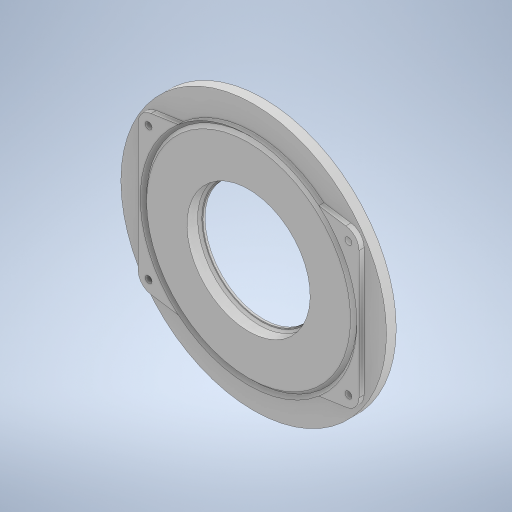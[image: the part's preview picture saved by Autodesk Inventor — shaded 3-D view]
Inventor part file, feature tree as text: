
AUTODESK INVENTOR PART (.ipt)
format: ipt  version: 2023.4 (Build 274418000, 418)  size: 462,336 bytes
history: native  units: mm
features: extrude x14, sketch x8, projected_geometry x3, chamfer x2, mirror x1
ambient origin geometry x8: Origin, YZ Plane, XZ Plane, XY Plane, X Axis, Y Axis, Z Axis, Center Point
bodies: Solid1 (feature_tree)
feature tree (28):
  extrude  "Extrusion1"  Depth=18.0mm TaperAngle=0.0deg
  extrude  "Extrusion5"  Depth=58.0mm
  extrude  "Extrusion8"  Depth=1.5mm
  extrude  "Extrusion9"  Depth=1.0mm TaperAngle=45.0deg
  chamfer  "Chamfer3"  Distance=2.2mm
  extrude  "Extrusion10"  Depth=3.2mm
  extrude  "Extrusion11"  Depth=3.2mm
  extrude  "Extrusion12"  Depth=6.0mm
  chamfer  "Chamfer4"  Distance=6.0mm
  extrude  "Extrusion15"  Depth=4.0mm TaperAngle=0.0deg
  extrude  "Extrusion16"  Depth=10.0mm
  extrude  "Extrusion17"  Depth=3.0mm
  extrude  "Extrusion18"  Depth=1.5mm TaperAngle=0.0deg
  extrude  "Extrusion19"  Depth=1.5mm TaperAngle=45.0deg
  extrude  "Extrusion20"  TaperAngle=0.0deg  [1 undecoded]
  extrude  "Extrusion21"  Depth=10.0mm
  mirror  "Mirror1"
  sketch  "Sketch1"  dims[d0=4.8mm d1=0.0mm d11=18.0mm d12=0.0mm]
  projected_geometry  "Projected Loop1"
  sketch  "Sketch17"  dims[d14=123.0mm d30=58.0mm]
  sketch  "Sketch19"  dims[d31=10.0mm d32=0.0mm d33=1.5mm]
  sketch  "Sketch20"  dims[d34=1.0mm d35=0.0mm d36=1.0mm d37=2.0mm d38=45.0deg d39=2.2mm d40=0.0mm]
  sketch  "Sketch21"  dims[d41=3.2mm d42=3.2mm]
  sketch  "Sketch22"  dims[d43=3.2mm d44=3.2mm]
  sketch  "Sketch23"  dims[d45=6.0mm d46=6.0mm]
  projected_geometry  "Projected Loop2"
  projected_geometry  "Projected Loop3"
  sketch  "Sketch24"  dims[d47=6.0mm d48=6.0mm d49=4.0mm d50=0.0mm d51=96.0mm d52=3.0mm d53=1.5mm d54=0.0mm d55=1.5mm d56=2.0mm d57=45.0deg d65=0.0mm d66=0.0mm d67=130.0mm d68=4.1mm d69=8.0mm d70=45.0deg d71=10.0mm d72=0.0mm d73=2.4mm d74=0.0mm d75=10.0mm d76=0.0mm d77=1.0mm d78=10.0mm d79=0.0mm d80=10.0mm d81=0.0mm d82=10.0mm d83=0.0mm]
note: 1 required parameter value undecoded (feature->parameter linkage not recoverable at this tier; creation-order binding heuristic only, values carry confidence <= 0.55)
